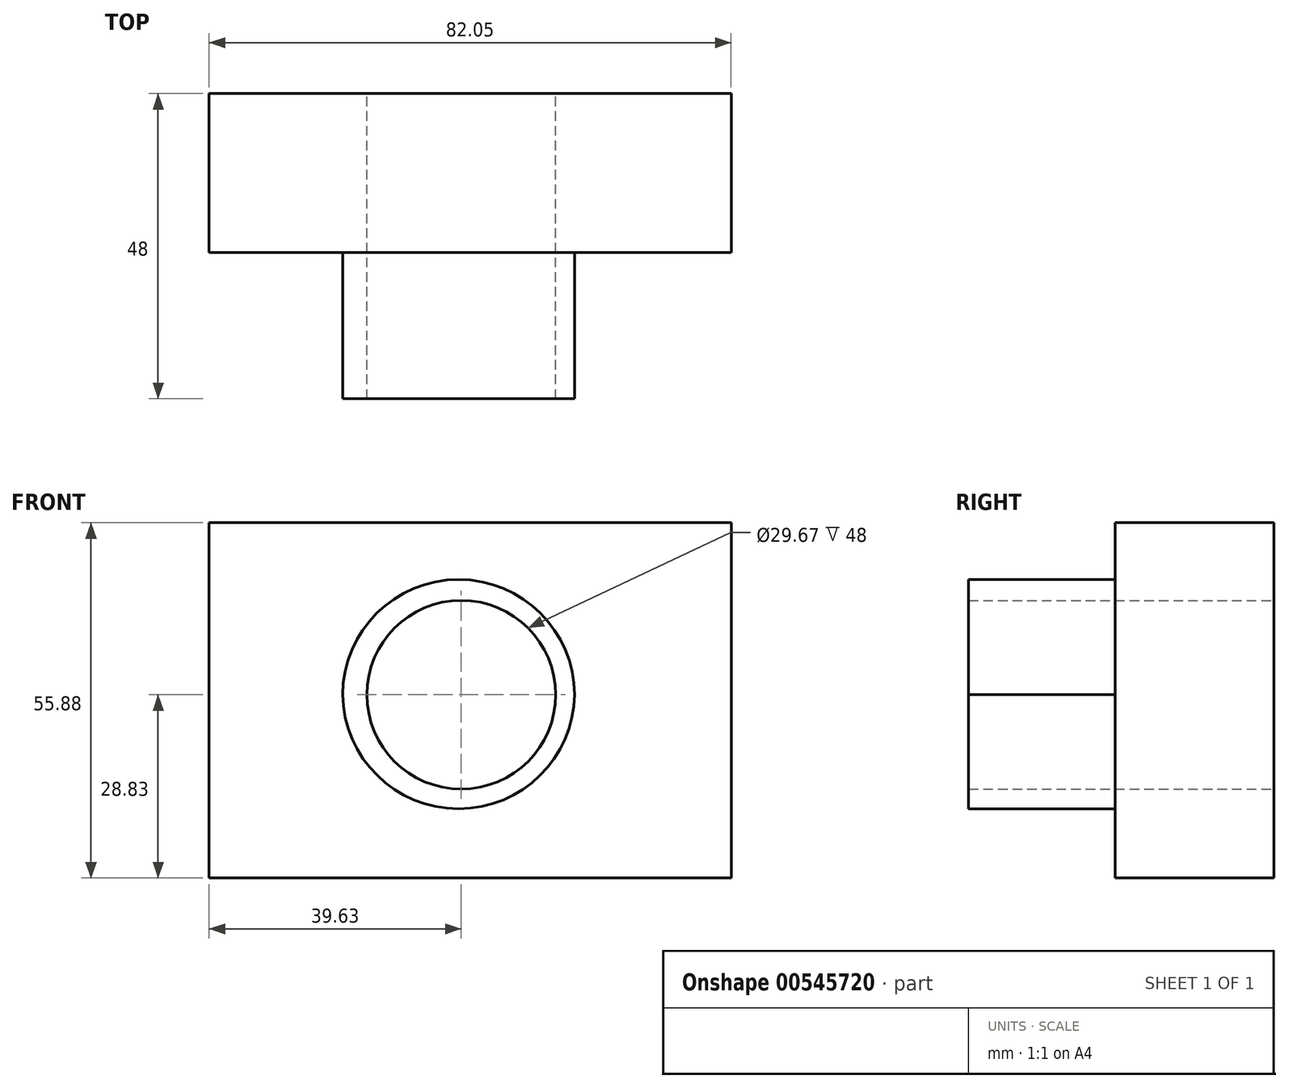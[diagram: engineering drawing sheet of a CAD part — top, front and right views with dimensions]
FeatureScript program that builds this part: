
annotation { "Feature Type Name" : "Feature", "Feature Type Description" : "" }
export const myFeature = defineFeature(function(context is Context, id is Id, definition is map)
    precondition{}
    {
        {
            var Q0;
            Q0=qCreatedBy(makeId("Front.planeOp"),FACE);
            var sketch = newSketch(context, id + "F0", { "sketchPlane" : qUnion([Q0])});
            skLineSegment(sketch, "E0.bottom", {"start": v(-39.63, 27.05) * mm, "end": v(42.42, 27.05) * mm});
            skLineSegment(sketch, "E0.top", {"start": v(-39.63, -28.83) * mm, "end": v(42.42, -28.83) * mm});
            skLineSegment(sketch, "E0.left", {"start": v(-39.63, 27.05) * mm, "end": v(-39.63, -28.83) * mm});
            skLineSegment(sketch, "E0.right", {"start": v(42.42, 27.05) * mm, "end": v(42.42, -28.83) * mm});
            skCircle(sketch, "E1", {"center": v(0, 0) * mm, "radius": 14.07 * mm});
            skSolve(sketch);
        }
        {
            var Q0;
            Q0 = qSketchRegion(id + "F0", true);
            extrude(context, id + "F1", {"entities" : qUnion([Q0]), "depth" : 25 * mm, "offsetDistance" : 25 * mm});
        }
        {
            var Q0;
            Q0=qCreatedBy(makeId("Front.planeOp"),FACE);
            var sketch = newSketch(context, id + "F2", { "sketchPlane" : qUnion([Q0])});
            skArc(sketch, "E2", {"start": v(17.82, 0) * mm, "mid": v(-0.41, 18.12) * mm, "end": v(-18.65, 0) * mm});
            skArc(sketch, "E3", {"start": v(-18.65, 0) * mm, "mid": v(-0.41, -17.94) * mm, "end": v(17.82, 0) * mm});
            skSolve(sketch);
        }
        {
            var Q0;
            Q0 = qSketchRegion(id + "F2", true);
            extrude(context, id + "F3", {"entities" : qUnion([Q0]), "operationType" : NewBodyOperationType.ADD, "depth" : 48 * mm, "offsetDistance" : 25 * mm});
        }
        {
            var Q0;
            Q0=qCreatedBy(makeId("Front.planeOp"),FACE);
            var sketch = newSketch(context, id + "F4", { "sketchPlane" : qUnion([Q0])});
            skCircle(sketch, "E4", {"center": v(0, 0) * mm, "radius": 14.84 * mm});
            skSolve(sketch);
        }
        {
            var Q0;
            Q0 = qSketchRegion(id + "F4", true);
            extrude(context, id + "F5", {"entities" : qUnion([Q0]), "operationType" : NewBodyOperationType.REMOVE, "depth" : 49 * mm, "offsetDistance" : 25 * mm});
        }
    });
